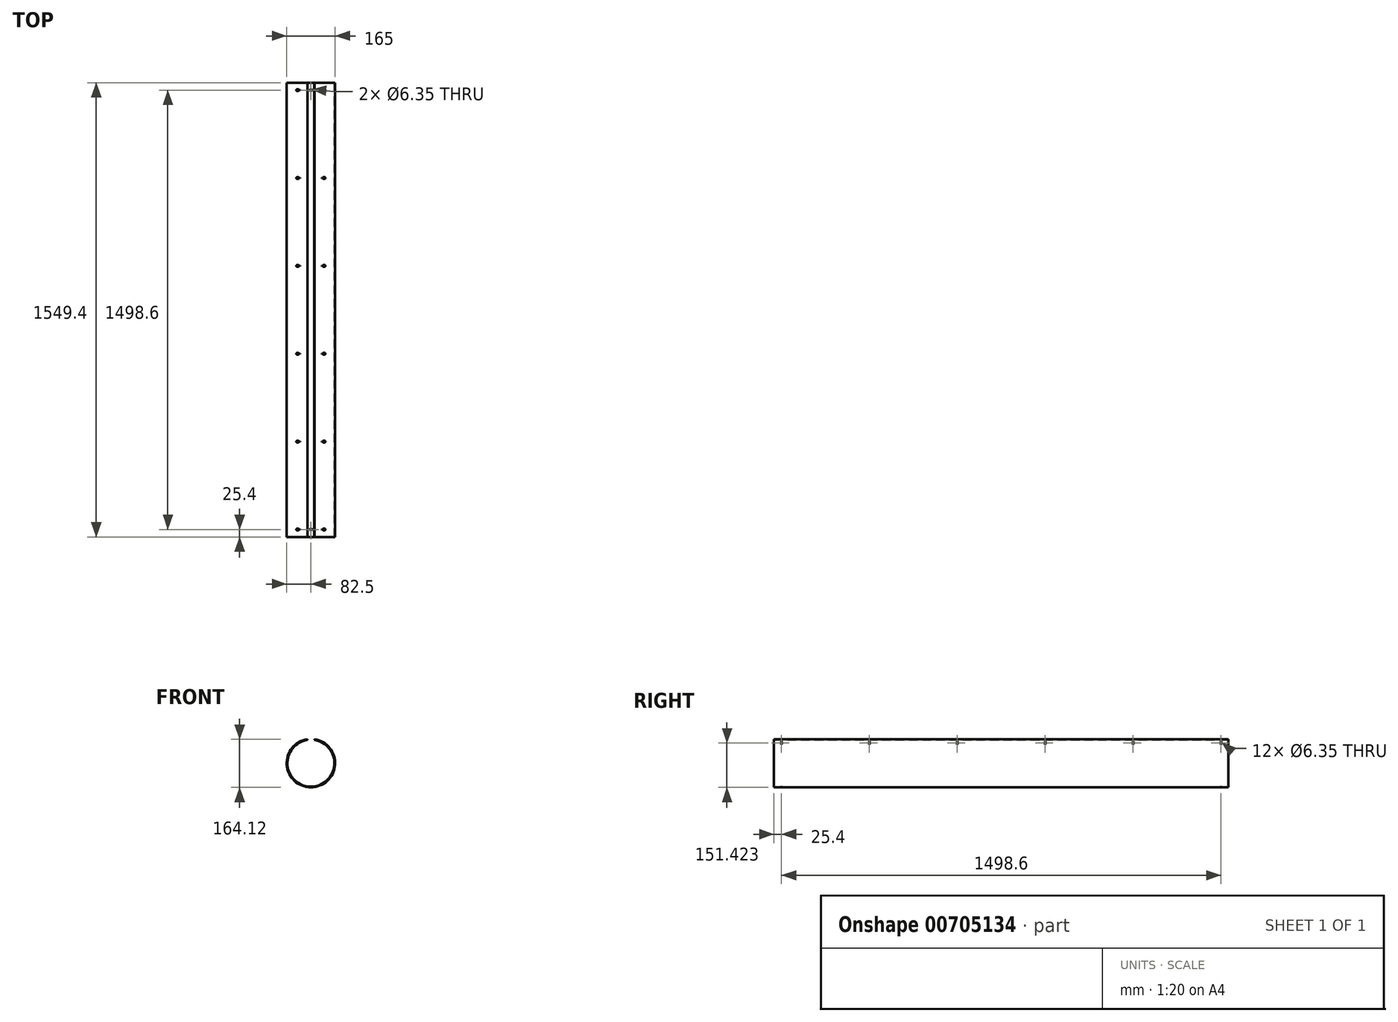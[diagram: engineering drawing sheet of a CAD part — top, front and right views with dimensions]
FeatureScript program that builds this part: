
annotation { "Feature Type Name" : "Feature", "Feature Type Description" : "" }
export const myFeature = defineFeature(function(context is Context, id is Id, definition is map)
    precondition{}
    {
        {
            var Q0;
            Q0=qCreatedBy(makeId("Front.planeOp"),FACE);
            var sketch = newSketch(context, id + "F0", { "sketchPlane" : qUnion([Q0])});
            skArc(sketch, "E0", {"start": v(-11.64, 79.15) * mm, "mid": v(0, -80) * mm, "end": v(11.64, 79.15) * mm});
            skArc(sketch, "E1", {"start": v(-12, 81.62) * mm, "mid": v(0, -82.5) * mm, "end": v(12, 81.62) * mm});
            skLineSegment(sketch, "E2", {"start": v(11.64, 79.15) * mm, "end": v(12, 81.62) * mm});
            skLineSegment(sketch, "E3", {"start": v(-11.64, 79.15) * mm, "end": v(-12, 81.62) * mm});
            skPoint(sketch, "E4.end.orphan", {"position": v(0, 82.5) * mm});
            skSolve(sketch);
        }
        {
            var Q0;
            Q0 = qSketchRegion(id + "F0", true);
            extrude(context, id + "F1", {"entities" : qUnion([Q0]), "depth" : 1549.4 * mm, "offsetDistance" : 25.4 * mm});
        }
        {
            var Q0;
            Q0=qCreatedBy(makeId("Top.planeOp"),FACE);
            var sketch = newSketch(context, id + "F2", { "sketchPlane" : qUnion([Q0])});
            skCircle(sketch, "E5", {"center": v(0, -25.4) * mm, "radius": 3.18 * mm});
            skCircle(sketch, "E6", {"center": v(0, -1524) * mm, "radius": 3.17 * mm});
            skSolve(sketch);
        }
        {
            var Q0;
            Q0 = qSketchRegion(id + "F2", true);
            extrude(context, id + "F3", {"entities" : qUnion([Q0]), "operationType" : NewBodyOperationType.REMOVE, "endBound" : BoundingType.SYMMETRIC, "oppositeDirection" : true, "depth" : 254 * mm, "offsetDistance" : 25.4 * mm});
        }
        {
            var Q0;
            Q0=qCreatedBy(makeId("Right.planeOp"),FACE);
            var sketch = newSketch(context, id + "F4", { "sketchPlane" : qUnion([Q0])});
            skLineSegment(sketch, "E7.0", {"start": v(-1549.4, 81.62) * mm, "end": v(0, 81.62) * mm, "construction": true});
            skLineSegment(sketch, "E8", {"start": v(0, 81.62) * mm, "end": v(0, 68.92) * mm, "construction": true});
            skCircle(sketch, "E9", {"center": v(-25.4, 68.92) * mm, "radius": 3.17 * mm});
            skCircle(sketch, "E10", {"center": v(-325.12, 68.92) * mm, "radius": 3.17 * mm});
            skCircle(sketch, "E11", {"center": v(-624.84, 68.92) * mm, "radius": 3.17 * mm});
            skCircle(sketch, "E12", {"center": v(-924.56, 68.92) * mm, "radius": 3.18 * mm});
            skCircle(sketch, "E13", {"center": v(-1224.28, 68.92) * mm, "radius": 3.18 * mm});
            skCircle(sketch, "E14", {"center": v(-1524, 68.92) * mm, "radius": 3.17 * mm});
            skSolve(sketch);
        }
        {
            var Q0;
            Q0 = qSketchRegion(id + "F4", true);
            extrude(context, id + "F5", {"entities" : qUnion([Q0]), "operationType" : NewBodyOperationType.REMOVE, "endBound" : BoundingType.SYMMETRIC, "oppositeDirection" : true, "depth" : 254 * mm, "offsetDistance" : 25.4 * mm});
        }
    });
